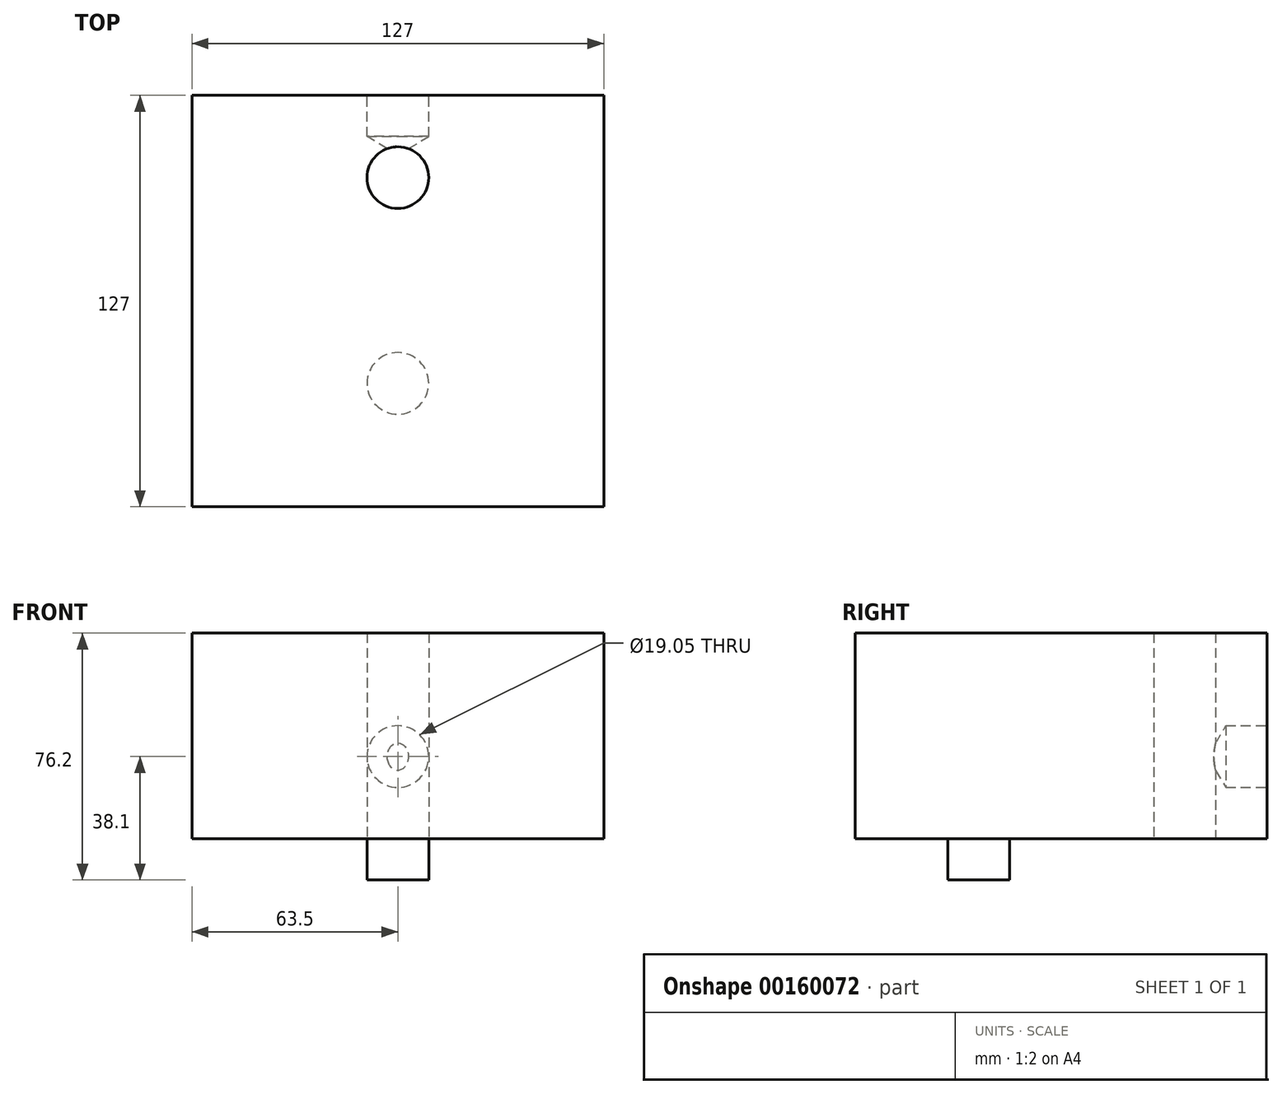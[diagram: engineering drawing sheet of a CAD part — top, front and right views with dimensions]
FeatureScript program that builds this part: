
annotation { "Feature Type Name" : "Feature", "Feature Type Description" : "" }
export const myFeature = defineFeature(function(context is Context, id is Id, definition is map)
    precondition{}
    {
        {
            var Q0;
            Q0=qCreatedBy(makeId("Front.planeOp"),FACE);
            var sketch = newSketch(context, id + "F0", { "sketchPlane" : qUnion([Q0])});
            skLineSegment(sketch, "E0.bottom", {"start": v(0, 0) * mm, "end": v(-127, 0) * mm});
            skLineSegment(sketch, "E0.top", {"start": v(0, 63.5) * mm, "end": v(-127, 63.5) * mm});
            skLineSegment(sketch, "E0.left", {"start": v(0, 0) * mm, "end": v(0, 63.5) * mm});
            skLineSegment(sketch, "E0.right", {"start": v(-127, 0) * mm, "end": v(-127, 63.5) * mm});
            skSolve(sketch);
        }
        {
            var Q0;
            Q0=makeQuery(id+"F0.imprint","IMPRINT",FACE,{"disambiguationData":[TD([[makeQuery(id+"F0.imprint","IMPRINT",EDGE,{"derivedFrom":sQuery(id+"F0.wireOp",EDGE,"E0.bottom")}),-1.0]])]});
            extrude(context, id + "F1", {"entities" : qUnion([Q0]), "depth" : 127 * mm});
        }
        {
            var Q0;
            Q0=makeQuery(id+"F1.opExtrude","SWEPT_FACE",FACE,{"disambiguationData":[OSD([sQuery(id+"F0.wireOp",EDGE,"E0.bottom")])]});
            var sketch = newSketch(context, id + "F2", { "sketchPlane" : qUnion([Q0])});
            skLineSegment(sketch, "E1.bottom", {"start": v(-127, 0) * mm, "end": v(0, 0) * mm});
            skLineSegment(sketch, "E1.top", {"start": v(-127, 50.8) * mm, "end": v(0, 50.8) * mm});
            skLineSegment(sketch, "E1.left", {"start": v(-127, 0) * mm, "end": v(-127, 50.8) * mm});
            skLineSegment(sketch, "E1.right", {"start": v(0, 0) * mm, "end": v(0, 50.8) * mm});
            skPoint(sketch, "E2", {"position": v(-63.5, 25.4) * mm});
            skPoint(sketch, "E2.positionSnap0", {"position": v(-63.5, 50.8) * mm});
            skPoint(sketch, "E2.positionSnap1", {"position": v(-127, 25.4) * mm});
            skSolve(sketch);
        }
        {
            var Q0;
            Q0=sQuery(id+"F2.wireOp",VERTEX,"E2");
            var Q1;
            Q1=makeQuery(id+"F1.opExtrude","SWEPT_BODY",BODY,{"disambiguationData":[OSD([sQuery(id+"F0.wireOp",EDGE,"E0.bottom"),sQuery(id+"F0.wireOp",EDGE,"E0.top"),sQuery(id+"F0.wireOp",EDGE,"E0.left"),sQuery(id+"F0.wireOp",EDGE,"E0.right")])]});
            hole(context, id + "F3", {"style" : HoleStyle.SIMPLE, "endStyle" : HoleEndStyle.THROUGH, "holeDiameter" : 19.05 * mm, "locations" : qUnion([Q0]), "scope" : qUnion([Q1]), "isTappedThrough" : true});
        }
        {
            var Q0;
            Q0=makeQuery(id+"F1.opExtrude","SWEPT_FACE",FACE,{"disambiguationData":[OSD([sQuery(id+"F0.wireOp",EDGE,"E0.bottom")])]});
            var sketch = newSketch(context, id + "F4", { "sketchPlane" : qUnion([Q0])});
            skLineSegment(sketch, "E3.bottom", {"start": v(-127, 127) * mm, "end": v(0, 127) * mm});
            skLineSegment(sketch, "E3.top", {"start": v(-127, 63.5) * mm, "end": v(0, 63.5) * mm});
            skLineSegment(sketch, "E3.left", {"start": v(-127, 127) * mm, "end": v(-127, 63.5) * mm});
            skLineSegment(sketch, "E3.right", {"start": v(0, 127) * mm, "end": v(0, 63.5) * mm});
            skLineSegment(sketch, "E4.top", {"start": v(-127, 114.3) * mm, "end": v(0, 114.3) * mm});
            skLineSegment(sketch, "E4.left", {"start": v(-127, 63.5) * mm, "end": v(-127, 114.3) * mm});
            skLineSegment(sketch, "E4.right", {"start": v(0, 63.5) * mm, "end": v(0, 114.3) * mm});
            skCircle(sketch, "E5", {"center": v(-63.5, 88.9) * mm, "radius": 9.52 * mm});
            skPoint(sketch, "E5.centerSnap0", {"position": v(-63.5, 114.3) * mm});
            skPoint(sketch, "E5.centerSnap1", {"position": v(-127, 88.9) * mm});
            skSolve(sketch);
        }
        {
            var Q0;
            Q0=makeQuery(id+"F4.imprint","IMPRINT",FACE,{"disambiguationData":[TD([[makeQuery(id+"F4.imprint","IMPRINT",EDGE,{"derivedFrom":sQuery(id+"F4.wireOp",EDGE,"E5")}),1.0]])]});
            extrude(context, id + "F5", {"entities" : qUnion([Q0]), "operationType" : NewBodyOperationType.ADD, "depth" : 12.7 * mm});
        }
        {
            var Q0;
            Q0=makeQuery(id+"F1.opExtrude","CAP_FACE",FACE,{"disambiguationData":[OSD([sQuery(id+"F0.wireOp",EDGE,"E0.bottom"),sQuery(id+"F0.wireOp",EDGE,"E0.top"),sQuery(id+"F0.wireOp",EDGE,"E0.left"),sQuery(id+"F0.wireOp",EDGE,"E0.right")])],"isStart":true});
            var sketch = newSketch(context, id + "F6", { "sketchPlane" : qUnion([Q0])});
            skLineSegment(sketch, "E6.bottom", {"start": v(0, 0) * mm, "end": v(127, 0) * mm});
            skLineSegment(sketch, "E6.top", {"start": v(0, 50.8) * mm, "end": v(127, 50.8) * mm});
            skLineSegment(sketch, "E6.left", {"start": v(0, 0) * mm, "end": v(0, 50.8) * mm});
            skLineSegment(sketch, "E6.right", {"start": v(127, 0) * mm, "end": v(127, 50.8) * mm});
            skPoint(sketch, "E7", {"position": v(63.5, 25.4) * mm});
            skPoint(sketch, "E7.positionSnap0", {"position": v(63.5, 50.8) * mm});
            skPoint(sketch, "E7.positionSnap1", {"position": v(0, 25.4) * mm});
            skSolve(sketch);
        }
        {
            var Q0;
            Q0=sQuery(id+"F6.wireOp",VERTEX,"E7");
            var Q1;
            Q1=makeQuery(id+"F1.opExtrude","SWEPT_BODY",BODY,{"disambiguationData":[OSD([sQuery(id+"F0.wireOp",EDGE,"E0.bottom"),sQuery(id+"F0.wireOp",EDGE,"E0.top"),sQuery(id+"F0.wireOp",EDGE,"E0.left"),sQuery(id+"F0.wireOp",EDGE,"E0.right")])]});
            hole(context, id + "F7", {"style" : HoleStyle.SIMPLE, "endStyle" : HoleEndStyle.BLIND, "holeDiameter" : 19.05 * mm, "holeDepth" : 12.7 * mm, "locations" : qUnion([Q0]), "scope" : qUnion([Q1])});
        }
    });
